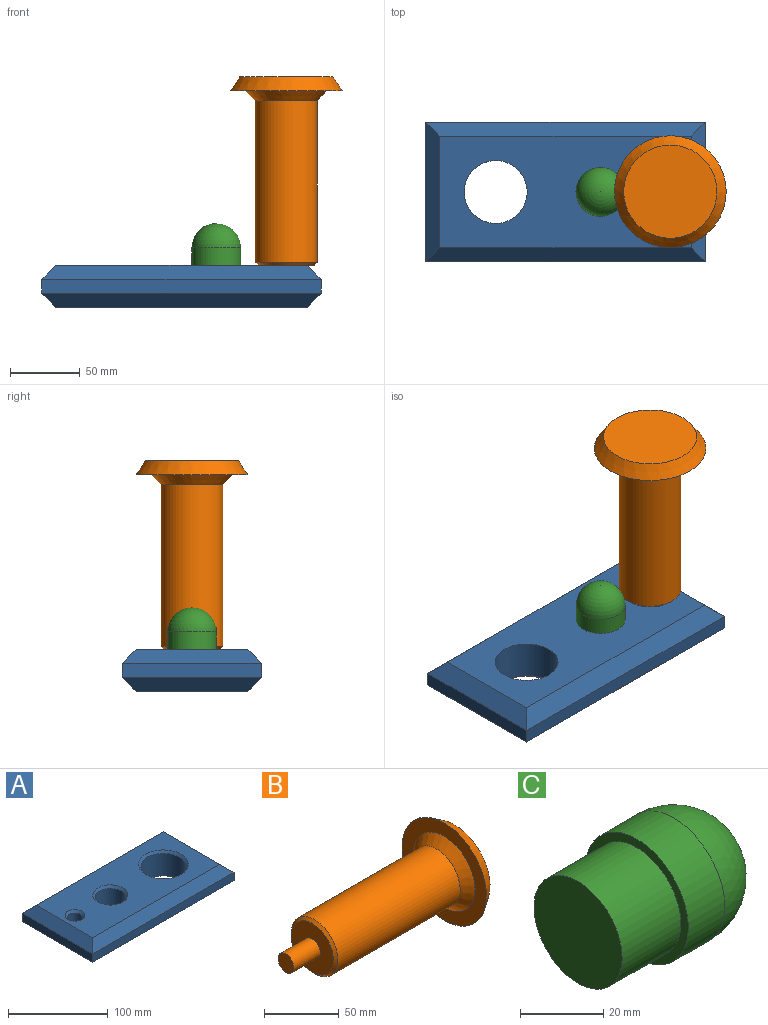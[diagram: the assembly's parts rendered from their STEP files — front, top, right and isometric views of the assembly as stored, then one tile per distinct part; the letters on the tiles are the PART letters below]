
ASSEMBLY  parts=3 mates=2
PART A: 20 faces, bbox 200x100x30 mm
  f0: plane 100x10mm, normal (-1,0,0), area 1000mm2, adj f1,f3,f9,f13
  f1: plane 200x10mm, normal (0,-1,0), area 2000mm2, adj f0,f2,f8,f12
  f2: plane 100x10mm, normal (1,0,0), area 1000mm2, adj f1,f3,f6,f10
  f3: plane 200x10mm, normal (0,1,0), area 2000mm2, adj f0,f2,f7,f11
  f4: plane 180x80mm, normal (0,0,1), area 11160.2mm2, adj f6,f7,f8,f9,f17,f18,f19
  f5: plane 180x80mm, normal (0,0,-1), area 11926mm2, adj f10,f11,f12,f13,f14,f15,f16
  f6: plane 100x10mm, normal (0.71,0,0.71), area 1272.8mm2, adj f2,f4,f7,f8
  f7: plane 200x10mm, normal (0,0.71,0.71), area 2687mm2, adj f3,f4,f6,f9
  f8: plane 200x10mm, normal (0,-0.71,0.71), area 2687mm2, adj f1,f4,f6,f9
  f9: plane 100x10mm, normal (-0.71,0,0.71), area 1272.8mm2, adj f0,f4,f7,f8
  f10: plane 100x10mm, normal (0.71,0,-0.71), area 1272.8mm2, adj f2,f5,f11,f12
  f11: plane 200x10mm, normal (0,0.71,-0.71), area 2687mm2, adj f3,f5,f10,f13
  f12: plane 200x10mm, normal (0,-0.71,-0.71), area 2687mm2, adj f1,f5,f10,f13
  f13: plane 100x10mm, normal (-0.71,0,-0.71), area 1272.8mm2, adj f0,f5,f11,f12
  f14: cylinder r=22.5mm len=45mm, axis (0,0,1), area 3887.7mm2, adj f5,f17
  f15: cylinder r=15mm len=30mm, axis (0,0,1), area 2591.8mm2, adj f5,f18
  f16: cylinder r=7.5mm len=27.5mm, axis (0,0,1), area 1295.9mm2, adj f5,f19
  f17: cone r=22.5mm half-angle=45deg, axis (0,0,1), area 527.6mm2, adj f4,f14
  f18: cone r=15mm half-angle=45deg, axis (0,0,1), area 361mm2, adj f4,f15
  f19: cone r=7.5mm half-angle=45deg, axis (0,0,1), area 194.4mm2, adj f4,f16
PART B: 9 faces, bbox 160x80x80 mm
  f0: plane 15x15mm, normal (-1,0,0), area 176.7mm2, adj f1
  f1: cylinder r=7.5mm len=25mm, axis (1,0,0), area 1178.1mm2, adj f0,f2
  f2: plane 40x40mm, normal (-1,0,0), area 1079.9mm2, adj f1,f3
  f3: cone r=20mm half-angle=45deg, axis (1,0,0), area 397mm2, adj f2,f4
  f4: cylinder r=22.12mm len=115.81mm, axis (1,0,0), area 16096.4mm2, adj f3,f5
  f5: cone r=22.12mm half-angle=45deg, axis (1,0,0), area 1612.1mm2, adj f4,f6
  f6: plane 80x80mm, normal (-1,0,0), area 2349.3mm2, adj f5,f7
  f7: cone r=40mm half-angle=33.6deg, axis (-1,0,0), area 2765.9mm2, adj f6,f8
  f8: plane 66.73x66.73mm, normal (1,0,0), area 3497.5mm2, adj f7
PART C: 5 faces, bbox 50x35x35 mm
  f0: plane 30x30mm, normal (-1,0,0), area 706.9mm2, adj f1
  f1: cylinder r=15mm len=30mm, axis (-1,0,0), area 1885mm2, adj f0,f2
  f2: plane 35x35mm, normal (-1,0,0), area 255.3mm2, adj f1,f3
  f3: cylinder r=17.5mm len=35mm, axis (-1,0,0), area 1374.4mm2, adj f2,f4
  f4: sphere r=17.5mm, area 1924.2mm2, adj f3
PLACE A rot(axis=(0,-1,0),180deg) t=(352.82,146.28,106.14)mm
PLACE B rot(axis=(0,-1,0),90deg) t=(327.82,196.28,152.02)mm
PLACE C rot(axis=(0,-1,0),90deg) t=(277.82,196.28,106.37)mm
MATE planar B.f1 <-> A.f16  axis (0,0,-1) through (327.82,196.28,106.14)mm
MATE planar C.f1 <-> A.f15  axis (0,0,-1) through (277.82,196.28,106.14)mm
